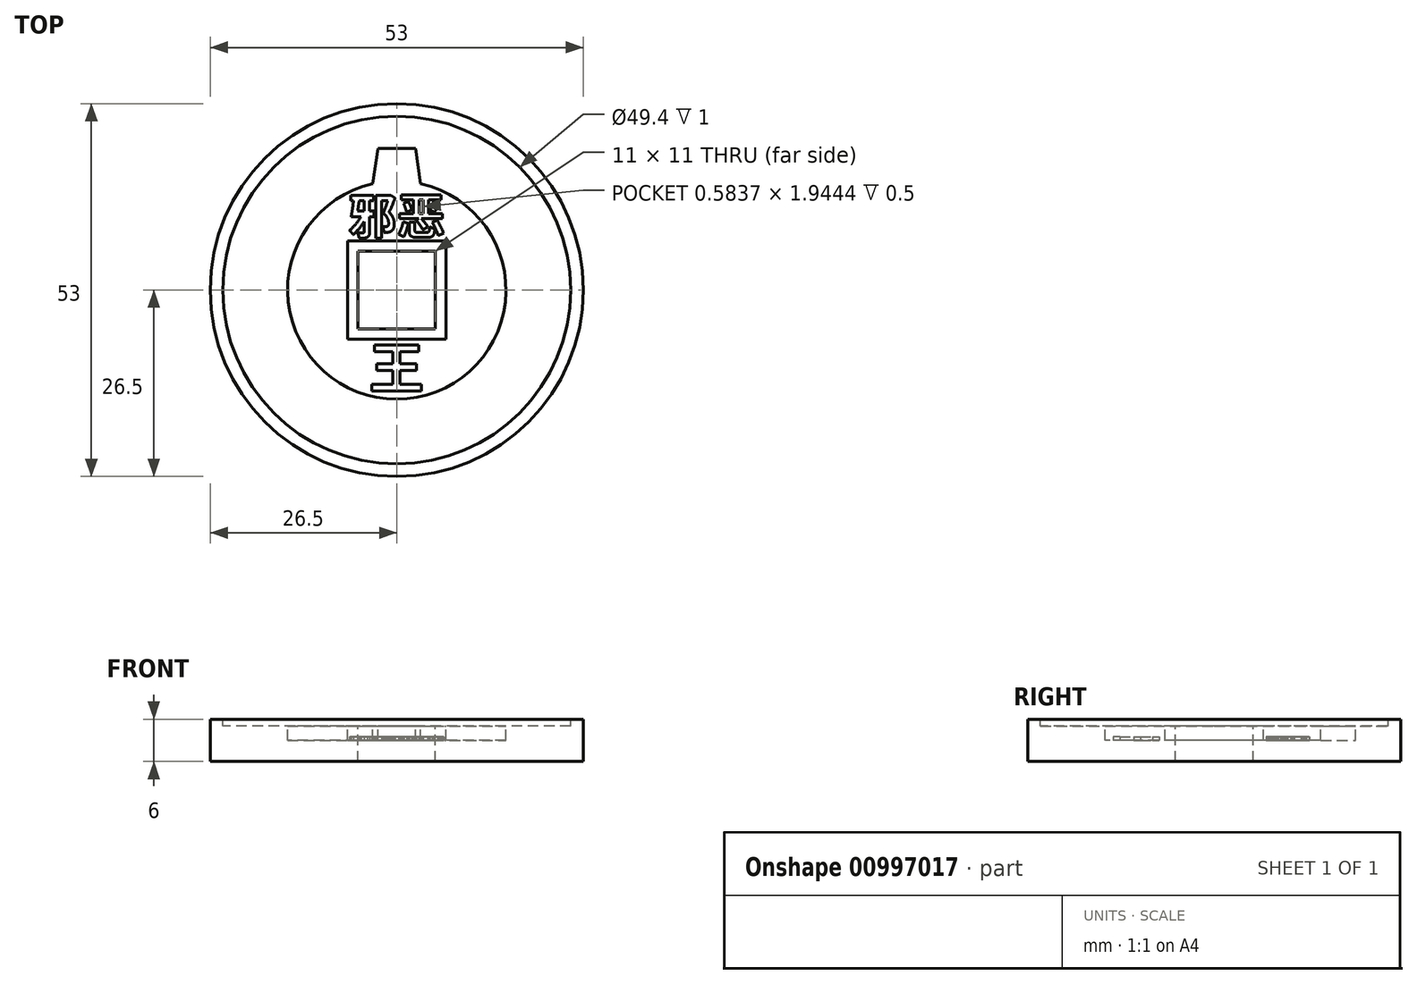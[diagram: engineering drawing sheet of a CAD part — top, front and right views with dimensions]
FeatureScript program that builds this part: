
annotation { "Feature Type Name" : "Feature", "Feature Type Description" : "" }
export const myFeature = defineFeature(function(context is Context, id is Id, definition is map)
    precondition{}
    {
        {
            var Q0;
            Q0=qCreatedBy(makeId("Front.planeOp"),FACE);
            var sketch = newSketch(context, id + "F0", { "sketchPlane" : qUnion([Q0])});
            skLineSegment(sketch, "E0.bottom", {"start": v(0, 0) * mm, "end": v(-26.5, 0) * mm});
            skLineSegment(sketch, "E0.top", {"start": v(-24.7, 6) * mm, "end": v(-26.5, 6) * mm});
            skLineSegment(sketch, "E0.left", {"start": v(0, 0) * mm, "end": v(0, 5) * mm});
            skLineSegment(sketch, "E0.right", {"start": v(-26.5, 0) * mm, "end": v(-26.5, 6) * mm});
            skLineSegment(sketch, "E1.bottom", {"start": v(0, 5) * mm, "end": v(-24.7, 5) * mm});
            skLineSegment(sketch, "E1.left", {"start": v(0, 5) * mm, "end": v(0, 1) * mm});
            skLineSegment(sketch, "E2", {"start": v(-24.7, 5) * mm, "end": v(-24.7, 6) * mm});
            skPoint(sketch, "E3.end.orphan", {"position": v(-23.2, 0) * mm});
            skSolve(sketch);
        }
        {
            var Q0;
            Q0 = qSketchRegion(id + "F0", true);
            var Q1;
            Q1=sQuery(id+"F0.wireOp",EDGE,"E1.left");
            revolve(context, id + "F1", {"surfaceOperationType" : NewSurfaceOperationType.NEW, "entities" : qUnion([Q0]), "axis" : qUnion([Q1]), "revolveType" : RevolveType.FULL});
        }
        {
            var Q0;
            Q0=qCreatedBy(makeId("Top.planeOp"),FACE);
            cPlane(context, id + "F2", {"entities" : qUnion([Q0]), "cplaneType" : CPlaneType.OFFSET, "offset" : 7 * mm, "width" : 150 * mm, "height" : 150 * mm});
        }
        {
            var Q0;
            Q0=qCreatedBy(id+"F2.planeOp",FACE);
            var sketch = newSketch(context, id + "F3", { "sketchPlane" : qUnion([Q0])});
            skLineSegment(sketch, "E4.bottom", {"start": v(-7, 7) * mm, "end": v(7, 7) * mm});
            skLineSegment(sketch, "E4.top", {"start": v(-7, -7) * mm, "end": v(-3.26, -7) * mm});
            skLineSegment(sketch, "E4.left", {"start": v(-7, 7) * mm, "end": v(-7, -7) * mm});
            skLineSegment(sketch, "E4.right", {"start": v(7, 7) * mm, "end": v(7, -7) * mm});
            skLineSegment(sketch, "E5.trimOffspring", {"start": v(3.26, -7) * mm, "end": v(7, -7) * mm});
            skLineSegment(sketch, "E6", {"start": v(-3.26, -7) * mm, "end": v(3.26, -7) * mm});
            skCircle(sketch, "E7", {"center": v(0, 0) * mm, "radius": 15.5 * mm});
            skSolve(sketch);
        }
        {
            var Q0;
            Q0=makeQuery(id+"F3.imprint","IMPRINT",FACE,{"disambiguationData":[TD([[makeQuery(id+"F3.imprint","IMPRINT",EDGE,{"derivedFrom":sQuery(id+"F3.wireOp",EDGE,"E4.bottom")}),1.0]])]});
            extrude(context, id + "F4", {"entities" : qUnion([Q0]), "operationType" : NewBodyOperationType.REMOVE, "oppositeDirection" : true, "depth" : 4 * mm, "offsetDistance" : 25 * mm});
        }
        {
            var Q0;
            Q0=qCreatedBy(id+"F2.planeOp",FACE);
            var sketch = newSketch(context, id + "F5", { "sketchPlane" : qUnion([Q0])});
            skLineSegment(sketch, "E8.bottom", {"start": v(-5.5, 5.5) * mm, "end": v(5.5, 5.5) * mm});
            skLineSegment(sketch, "E8.top", {"start": v(-5.5, -5.5) * mm, "end": v(5.5, -5.5) * mm});
            skLineSegment(sketch, "E8.left", {"start": v(-5.5, 5.5) * mm, "end": v(-5.5, -5.5) * mm});
            skLineSegment(sketch, "E8.right", {"start": v(5.5, 5.5) * mm, "end": v(5.5, -5.5) * mm});
            skSolve(sketch);
        }
        {
            var Q0;
            Q0 = qSketchRegion(id + "F5", true);
            extrude(context, id + "F6", {"entities" : qUnion([Q0]), "operationType" : NewBodyOperationType.REMOVE, "endBound" : BoundingType.THROUGH_ALL, "oppositeDirection" : true, "depth" : 25 * mm, "offsetDistance" : 25 * mm});
        }
        {
            var Q0;
            Q0=makeQuery(id+"F1.opRevolve","SWEPT_FACE",FACE,{"disambiguationData":[OSD([sQuery(id+"F0.wireOp",EDGE,"E1.bottom")])]});
            var sketch = newSketch(context, id + "F7", { "sketchPlane" : qUnion([Q0])});
            skLineSegment(sketch, "E9", {"start": v(-3.4, 15.12) * mm, "end": v(0, 15.12) * mm});
            skLineSegment(sketch, "E10", {"start": v(-3.4, 15.12) * mm, "end": v(-2.69, 20.1) * mm});
            skLineSegment(sketch, "E11", {"start": v(-2.69, 20.1) * mm, "end": v(0, 20.1) * mm});
            skLineSegment(sketch, "E12.MirrorCS", {"start": v(2.69, 20.1) * mm, "end": v(0, 20.1) * mm});
            skLineSegment(sketch, "E13.MirrorCS", {"start": v(3.4, 15.12) * mm, "end": v(2.69, 20.1) * mm});
            skLineSegment(sketch, "E14.MirrorCS", {"start": v(3.4, 15.12) * mm, "end": v(0, 15.12) * mm});
            skSolve(sketch);
        }
        {
            var Q0;
            Q0 = qSketchRegion(id + "F7", true);
            extrude(context, id + "F8", {"entities" : qUnion([Q0]), "operationType" : NewBodyOperationType.REMOVE, "oppositeDirection" : true, "depth" : 2 * mm, "offsetDistance" : 25 * mm});
        }
        {
            var Q0;
            Q0=qCreatedBy(makeId("Top.planeOp"),FACE);
            var sketch = newSketch(context, id + "F9", { "sketchPlane" : qUnion([Q0])});
            skText(sketch, "E15", { "text": "邪恶", "fontName": "NotoSansCJKtc-Bold.otf"});
            skText(sketch, "E16", { "text": "王", "fontName": "NotoSansCJKtc-Bold.otf"});
            const initialGuessF9  = {"E15": [-0.00696, 0.00796, 1, 0, 0.005], "E16": [-0.00396, -0.01399, 1, 0, 0.00564]};
            skSetInitialGuess(sketch, initialGuessF9);
            skSolve(sketch);
        }
        {
            var Q0;
            Q0 = qSketchRegion(id + "F9", true);
            extrude(context, id + "F10", {"entities" : qUnion([Q0]), "operationType" : NewBodyOperationType.ADD, "depth" : 3.5 * mm, "offsetDistance" : 25 * mm});
        }
    });
